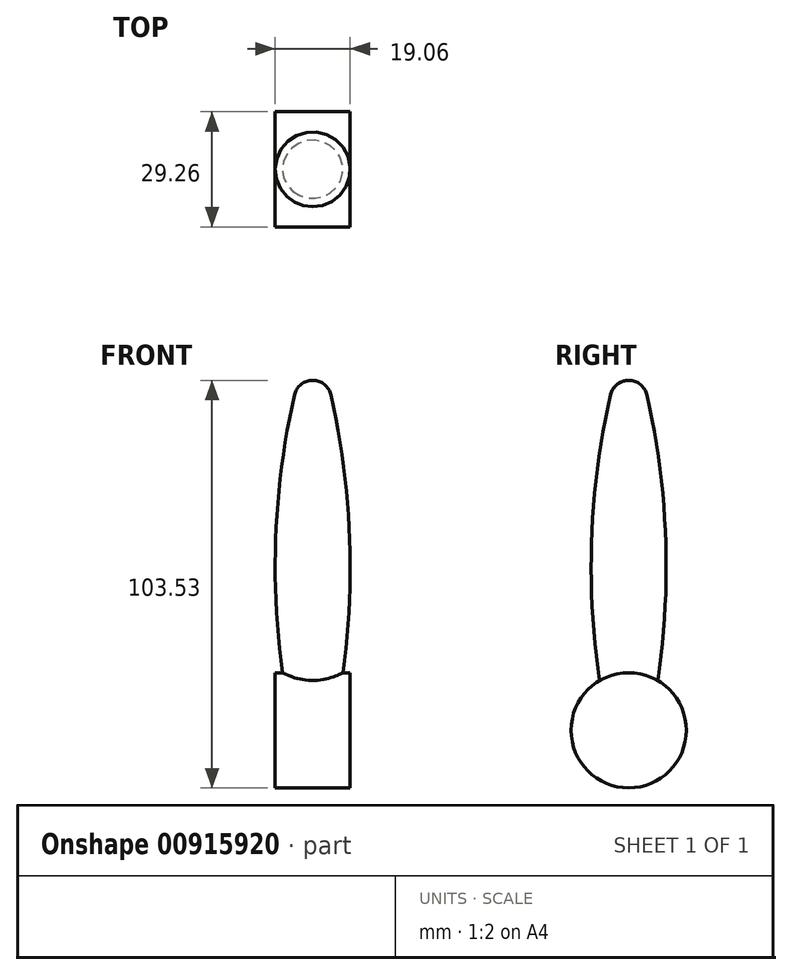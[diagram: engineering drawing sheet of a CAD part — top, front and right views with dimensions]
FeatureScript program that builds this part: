
annotation { "Feature Type Name" : "Feature", "Feature Type Description" : "" }
export const myFeature = defineFeature(function(context is Context, id is Id, definition is map)
    precondition{}
    {
        {
            var Q0;
            Q0=qCreatedBy(makeId("Right.planeOp"),FACE);
            var sketch = newSketch(context, id + "F0", { "sketchPlane" : qUnion([Q0])});
            skArc(sketch, "E0", {"start": v(-4.64, 85.2) * mm, "mid": v(-9.48, 45.86) * mm, "end": v(-6.35, 6.35) * mm});
            skLineSegment(sketch, "E1", {"start": v(-6.35, 6.35) * mm, "end": v(0, 6.35) * mm});
            skArc(sketch, "E2", {"start": v(0, 88.9) * mm, "mid": v(-2.97, 87.86) * mm, "end": v(-4.64, 85.2) * mm});
            skLineSegment(sketch, "E3", {"start": v(0, 88.9) * mm, "end": v(0, 6.35) * mm});
            skLineSegment(sketch, "E4", {"start": v(0, 0) * mm, "end": v(0, -8.71) * mm, "construction": true});
            skSolve(sketch);
        }
        {
            var Q0;
            Q0=makeQuery(id+"F0.imprint","IMPRINT",FACE,{"disambiguationData":[TD([[makeQuery(id+"F0.imprint","IMPRINT",EDGE,{"derivedFrom":sQuery(id+"F0.wireOp",EDGE,"E0")}),1.0]])]});
            var Q1;
            Q1=sQuery(id+"F0.wireOp",EDGE,"E3");
            revolve(context, id + "F1", {"surfaceOperationType" : NewSurfaceOperationType.NEW, "entities" : qUnion([Q0]), "axis" : qUnion([Q1]), "revolveType" : RevolveType.FULL});
        }
        {
            var Q0;
            Q0=qCreatedBy(makeId("Top.planeOp"),FACE);
            var sketch = newSketch(context, id + "F2", { "sketchPlane" : qUnion([Q0])});
            skLineSegment(sketch, "E5", {"start": v(0, 0) * mm, "end": v(0, 16.33) * mm});
            skSolve(sketch);
        }
        {
            var Q0;
            Q0=qCreatedBy(makeId("Right.planeOp"),FACE);
            var sketch = newSketch(context, id + "F3", { "sketchPlane" : qUnion([Q0])});
            skCircle(sketch, "E6", {"center": v(0, 0) * mm, "radius": 14.63 * mm});
            skSolve(sketch);
        }
        {
            var Q0;
            Q0 = qSketchRegion(id + "F3", true);
            extrude(context, id + "F4", {"entities" : qUnion([Q0]), "operationType" : NewBodyOperationType.ADD, "endBound" : BoundingType.SYMMETRIC, "depth" : 19.05 * mm, "offsetDistance" : 25.4 * mm});
        }
    });
